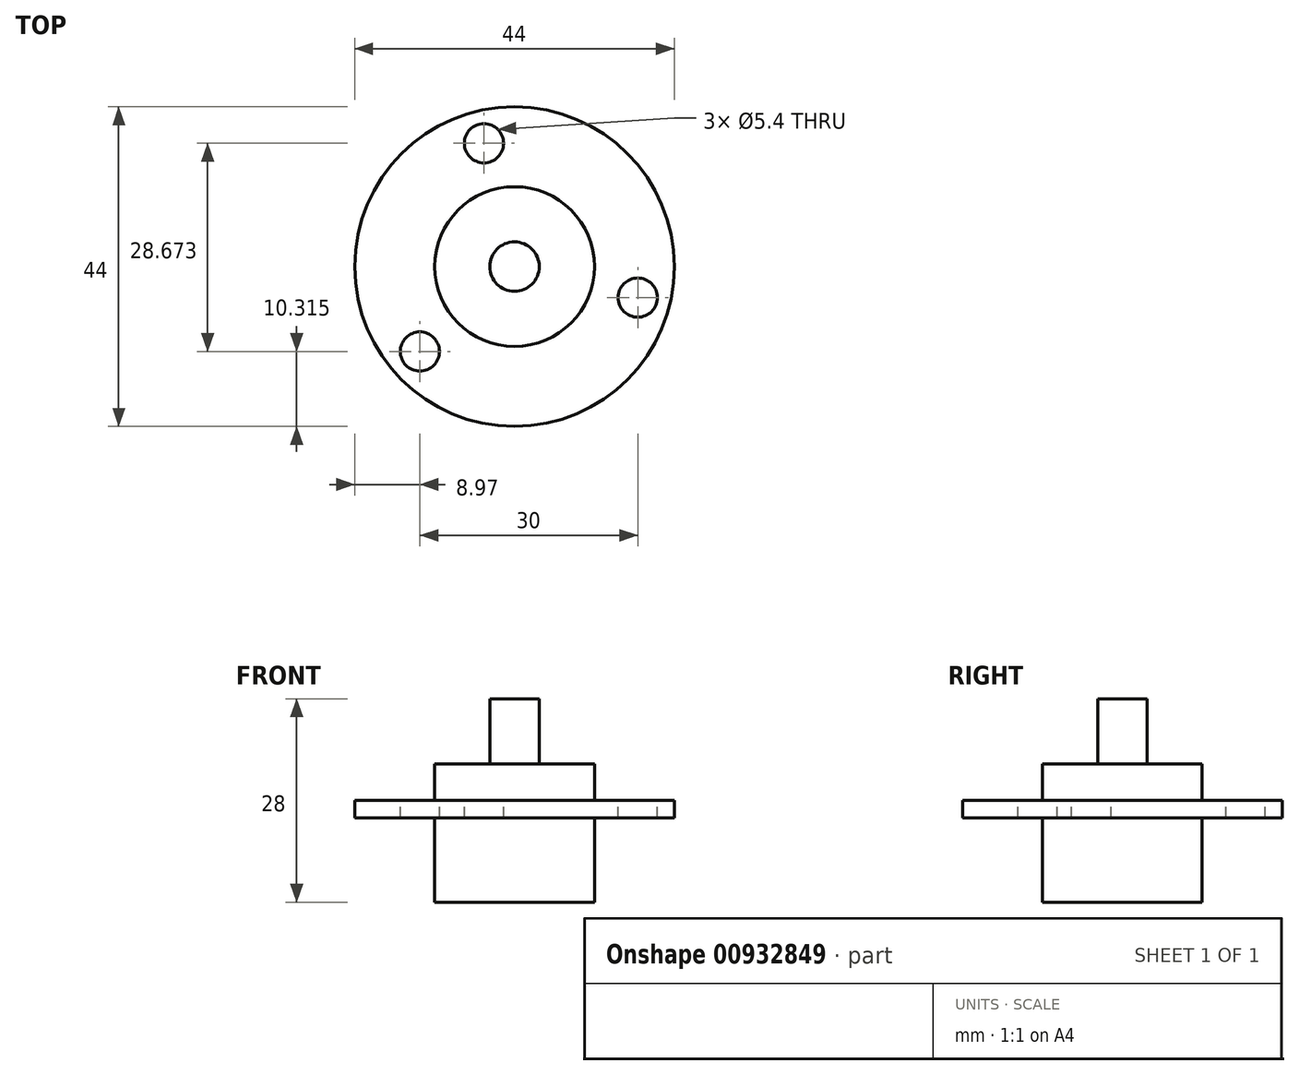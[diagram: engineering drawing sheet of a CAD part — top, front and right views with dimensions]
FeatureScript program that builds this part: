
annotation { "Feature Type Name" : "Feature", "Feature Type Description" : "" }
export const myFeature = defineFeature(function(context is Context, id is Id, definition is map)
    precondition{}
    {
        {
            var Q0;
            Q0=qCreatedBy(makeId("Front.planeOp"),FACE);
            var sketch = newSketch(context, id + "F0", { "sketchPlane" : qUnion([Q0])});
            skLineSegment(sketch, "E0", {"start": v(-130.51, -122.08) * mm, "end": v(-130.51, -110.48) * mm});
            skLineSegment(sketch, "E1", {"start": v(-130.51, -110.48) * mm, "end": v(-141.51, -110.48) * mm});
            skLineSegment(sketch, "E2", {"start": v(-141.51, -110.48) * mm, "end": v(-141.51, -108.08) * mm});
            skLineSegment(sketch, "E3", {"start": v(-141.51, -108.08) * mm, "end": v(-130.51, -108.08) * mm});
            skLineSegment(sketch, "E4", {"start": v(-130.51, -108.08) * mm, "end": v(-130.51, -103.08) * mm});
            skLineSegment(sketch, "E5", {"start": v(-130.51, -103.08) * mm, "end": v(-122.91, -103.08) * mm});
            skLineSegment(sketch, "E6", {"start": v(-122.91, -103.08) * mm, "end": v(-122.91, -94.08) * mm});
            skLineSegment(sketch, "E7", {"start": v(-122.91, -94.08) * mm, "end": v(-119.51, -94.08) * mm});
            skLineSegment(sketch, "E8", {"start": v(-119.51, -94.08) * mm, "end": v(-119.51, -122.08) * mm});
            skLineSegment(sketch, "E9", {"start": v(-119.51, -122.08) * mm, "end": v(-130.51, -122.08) * mm});
            skSolve(sketch);
        }
        {
            var Q0;
            Q0=makeQuery(id+"F0.imprint","IMPRINT",FACE,{"disambiguationData":[TD([[makeQuery(id+"F0.imprint","IMPRINT",EDGE,{"derivedFrom":sQuery(id+"F0.wireOp",EDGE,"E0")}),-1.0]])]});
            var Q1;
            Q1=sQuery(id+"F0.wireOp",EDGE,"E8");
            revolve(context, id + "F1", {"surfaceOperationType" : NewSurfaceOperationType.NEW, "entities" : qUnion([Q0]), "axis" : qUnion([Q1]), "revolveType" : RevolveType.FULL});
        }
        {
            var Q0;
            Q0=makeQuery(id+"F1.opRevolve","SWEPT_FACE",FACE,{"disambiguationData":[OSD([sQuery(id+"F0.wireOp",EDGE,"E3")])]});
            var sketch = newSketch(context, id + "F2", { "sketchPlane" : qUnion([Q0])});
            skCircle(sketch, "E10", {"center": v(-119.51, 0) * mm, "radius": 17.5 * mm});
            skCircle(sketch, "E11", {"center": v(-123.72, 16.99) * mm, "radius": 2.7 * mm});
            skCircle(sketch, "E12", {"center": v(-132.54, -11.69) * mm, "radius": 2.7 * mm});
            skCircle(sketch, "E13", {"center": v(-102.54, -4.26) * mm, "radius": 2.7 * mm});
            skSolve(sketch);
        }
        {
            var Q0;
            {var subQ0=sQuery(id+"F2.wireOp",EDGE,"E12");var subQ1=sQuery(id+"F2.wireOp",EDGE,"E10");var subQ2=makeQuery(id+"F2.imprint","INTERSECT",VERTEX,{"disambiguationData":[OD(0.0)],"derivedFrom":[subQ1,subQ0]});Q0=makeQuery(id+"F2.imprint","IMPRINT",FACE,{"disambiguationData":[TD([[makeQuery(id+"F2.imprint","IMPRINT",EDGE,{"disambiguationData":[TD([[subQ2,-1.0]])],"derivedFrom":subQ1}),-1.0]])]});}
            var Q1;
            {var subQ0=sQuery(id+"F2.wireOp",EDGE,"E12");var subQ1=sQuery(id+"F2.wireOp",EDGE,"E10");var subQ2=makeQuery(id+"F2.imprint","INTERSECT",VERTEX,{"disambiguationData":[OD(0.0)],"derivedFrom":[subQ1,subQ0]});Q1=makeQuery(id+"F2.imprint","IMPRINT",FACE,{"disambiguationData":[TD([[makeQuery(id+"F2.imprint","IMPRINT",EDGE,{"disambiguationData":[TD([[subQ2,-1.0]])],"derivedFrom":subQ1}),1.0]])]});}
            var Q2;
            {var subQ0=sQuery(id+"F2.wireOp",EDGE,"E11");var subQ1=sQuery(id+"F2.wireOp",EDGE,"E10");var subQ2=makeQuery(id+"F2.imprint","INTERSECT",VERTEX,{"disambiguationData":[OD(0.0)],"derivedFrom":[subQ1,subQ0]});Q2=makeQuery(id+"F2.imprint","IMPRINT",FACE,{"disambiguationData":[TD([[makeQuery(id+"F2.imprint","IMPRINT",EDGE,{"disambiguationData":[TD([[subQ2,1.0]])],"derivedFrom":subQ1}),-1.0]])]});}
            var Q3;
            {var subQ0=sQuery(id+"F2.wireOp",EDGE,"E11");var subQ1=sQuery(id+"F2.wireOp",EDGE,"E10");var subQ2=makeQuery(id+"F2.imprint","INTERSECT",VERTEX,{"disambiguationData":[OD(0.0)],"derivedFrom":[subQ1,subQ0]});Q3=makeQuery(id+"F2.imprint","IMPRINT",FACE,{"disambiguationData":[TD([[makeQuery(id+"F2.imprint","IMPRINT",EDGE,{"disambiguationData":[TD([[subQ2,1.0]])],"derivedFrom":subQ1}),1.0]])]});}
            var Q4;
            {var subQ0=sQuery(id+"F2.wireOp",EDGE,"E13");var subQ1=sQuery(id+"F2.wireOp",EDGE,"E10");var subQ2=makeQuery(id+"F2.imprint","INTERSECT",VERTEX,{"disambiguationData":[OD(0.0)],"derivedFrom":[subQ1,subQ0]});Q4=makeQuery(id+"F2.imprint","IMPRINT",FACE,{"disambiguationData":[TD([[makeQuery(id+"F2.imprint","IMPRINT",EDGE,{"disambiguationData":[TD([[subQ2,-1.0]])],"derivedFrom":subQ1}),-1.0]])]});}
            var Q5;
            {var subQ0=sQuery(id+"F2.wireOp",EDGE,"E13");var subQ1=sQuery(id+"F2.wireOp",EDGE,"E10");var subQ2=makeQuery(id+"F2.imprint","INTERSECT",VERTEX,{"disambiguationData":[OD(0.0)],"derivedFrom":[subQ1,subQ0]});Q5=makeQuery(id+"F2.imprint","IMPRINT",FACE,{"disambiguationData":[TD([[makeQuery(id+"F2.imprint","IMPRINT",EDGE,{"disambiguationData":[TD([[subQ2,-1.0]])],"derivedFrom":subQ1}),1.0]])]});}
            var Q6;
            Q6=makeQuery(id+"F1.opRevolve","SWEPT_FACE",FACE,{"disambiguationData":[OSD([sQuery(id+"F0.wireOp",EDGE,"E1")])]});
            extrude(context, id + "F3", {"entities" : qUnion([Q0, Q1, Q2, Q3, Q4, Q5]), "operationType" : NewBodyOperationType.REMOVE, "endBound" : BoundingType.UP_TO_SURFACE, "oppositeDirection" : true, "depth" : 25 * mm, "endBoundEntityFace" : qUnion([Q6]), "offsetDistance" : 25 * mm});
        }
    });
